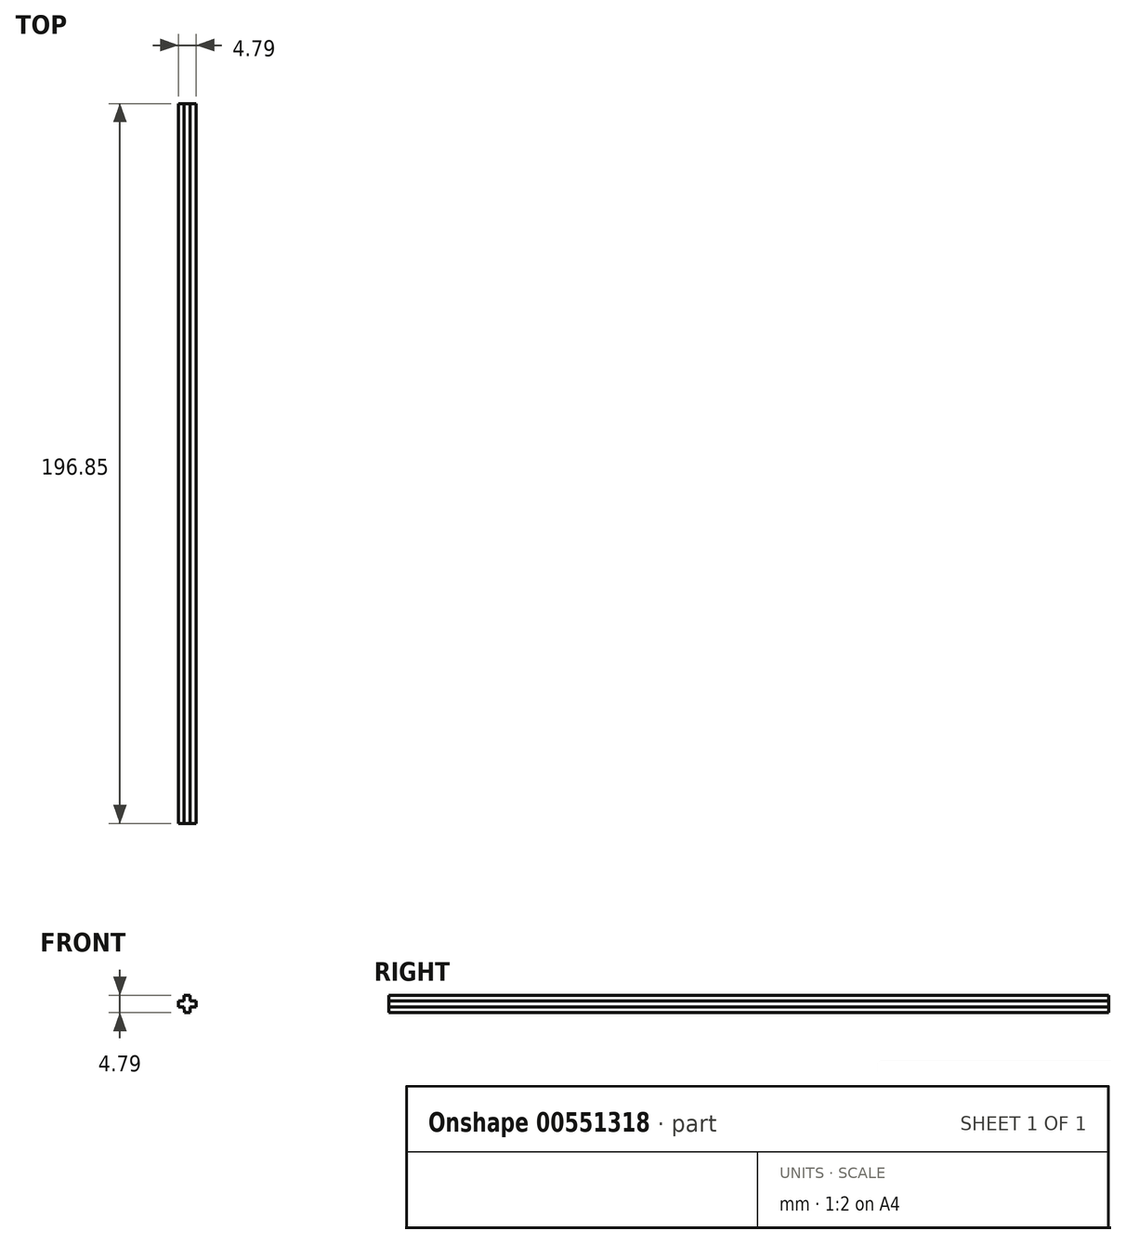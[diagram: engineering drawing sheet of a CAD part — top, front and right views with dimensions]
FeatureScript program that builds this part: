
annotation { "Feature Type Name" : "Feature", "Feature Type Description" : "" }
export const myFeature = defineFeature(function(context is Context, id is Id, definition is map)
    precondition{}
    {
        {
            var Q0;
            Q0=qCreatedBy(makeId("Front.planeOp"),FACE);
            var sketch = newSketch(context, id + "F0", { "sketchPlane" : qUnion([Q0])});
            skLineSegment(sketch, "E0", {"start": v(0, 0) * mm, "end": v(0, 1.59) * mm});
            skLineSegment(sketch, "E1", {"start": v(0, 0) * mm, "end": v(-1.59, 0) * mm});
            skLineSegment(sketch, "E2", {"start": v(0, 1.59) * mm, "end": v(1.6, 1.59) * mm});
            skLineSegment(sketch, "E3", {"start": v(1.6, 1.59) * mm, "end": v(1.6, 0) * mm});
            skLineSegment(sketch, "E4", {"start": v(1.6, 0) * mm, "end": v(0, 0) * mm});
            skLineSegment(sketch, "E5", {"start": v(0, 0) * mm, "end": v(0, -1.6) * mm});
            skLineSegment(sketch, "E6", {"start": v(0, -1.6) * mm, "end": v(1.62, -1.6) * mm});
            skLineSegment(sketch, "E7", {"start": v(1.62, -1.6) * mm, "end": v(1.6, 0) * mm});
            skLineSegment(sketch, "E8", {"start": v(0, -1.6) * mm, "end": v(0.02, -3.2) * mm});
            skLineSegment(sketch, "E9", {"start": v(1.62, -1.6) * mm, "end": v(1.63, -3.2) * mm});
            skLineSegment(sketch, "E10", {"start": v(1.63, -3.2) * mm, "end": v(0.02, -3.2) * mm});
            skLineSegment(sketch, "E11", {"start": v(-1.59, 0) * mm, "end": v(-1.57, -1.6) * mm});
            skLineSegment(sketch, "E12", {"start": v(-1.57, -1.6) * mm, "end": v(0, -1.6) * mm});
            skLineSegment(sketch, "E13", {"start": v(1.6, 0) * mm, "end": v(3.2, 0) * mm});
            skLineSegment(sketch, "E14", {"start": v(1.62, -1.6) * mm, "end": v(3.2, -1.58) * mm});
            skLineSegment(sketch, "E15", {"start": v(3.2, -1.58) * mm, "end": v(3.2, 0) * mm});
            skSolve(sketch);
        }
        {
            var Q0;
            Q0 = qSketchRegion(id + "F0", true);
            extrude(context, id + "F1", {"entities" : qUnion([Q0]), "depth" : 196.85 * mm, "offsetDistance" : 25.4 * mm});
        }
    });
